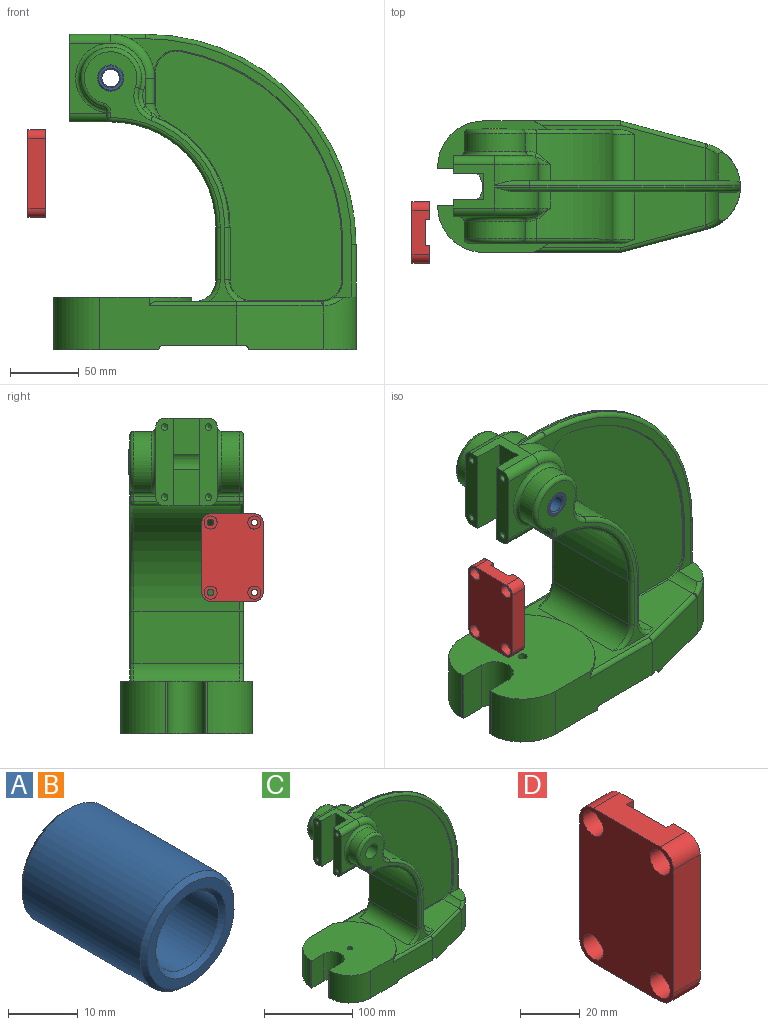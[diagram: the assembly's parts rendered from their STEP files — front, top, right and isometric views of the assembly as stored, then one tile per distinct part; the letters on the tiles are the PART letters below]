
ASSEMBLY  parts=4 mates=4
PART A: 8 faces, bbox 19.1x25.4x19.1 mm
  f0: plane 17.53x17.53mm, normal (0,-1,0), area 82.3mm2, adj f4,f5
  f1: plane 17.53x17.53mm, normal (0,1,0), area 82.3mm2, adj f6,f7
  f2: cylinder r=9.53mm len=23.88mm, axis (0,1,0), area 1428.9mm2, adj f4,f7
  f3: cylinder r=6.35mm len=23.88mm, axis (0,1,0), area 952.6mm2, adj f5,f6
  f4: cone r=9.53mm half-angle=45deg, axis (0,1,0), area 61.9mm2, adj f0,f2
  f5: cone r=6.35mm half-angle=45deg, axis (0,-1,0), area 45.6mm2, adj f0,f3
  f6: cone r=6.35mm half-angle=45deg, axis (0,1,0), area 45.6mm2, adj f1,f3
  f7: cone r=9.53mm half-angle=45deg, axis (0,-1,0), area 61.9mm2, adj f1,f2
PART B: same geometry as A
PART C: 180 faces, bbox 234.5x98.1x244 mm
  f0: plane 63.5x12.7mm, normal (-1,0,0), area 753.5mm2, adj f2,f15,f17,f92,f97,f149,f151,f158
  f1: plane 20.23x2.34mm, normal (0,1,0), area 23.9mm2, adj f90,f91,f104,f106
  f2: plane 50.8x30.1mm, normal (0,-1,0), area 515.4mm2, adj f0,f83,f92,f97,f124
  f3: plane 22.59x12.73mm, normal (1,0,0), area 235.4mm2, adj f19,f26,f32,f87,f94,f174
  f4: plane 22.59x12.73mm, normal (1,0,0), area 235.4mm2, adj f10,f14,f33,f86,f90,f164
  f5: plane 99.19x38.1mm, normal (0,-1,0), area 3202mm2, adj f6,f40,f46,f49,f52,f58,f76,f133
  f6: plane 100x95.25mm, normal (0,0,1), area 7398mm2, adj f5,f43,f44,f48,f54,f55,f56,f57
  f7: plane 38.1x34.96mm, normal (1,0,0), area 1331.9mm2, adj f8,f9,f114,f169
  f8: cylinder r=15.88mm len=34.96mm, axis (0,1,0), area 871.7mm2, adj f7,f37,f115,f167
  f9: cylinder r=85.72mm len=80.21mm, axis (0,1,0), area 3442.3mm2, adj f7,f80,f86,f100,f113,f168
  f10: cylinder r=15.88mm len=18.65mm, axis (0,1,0), area 22.7mm2, adj f4,f11,f33,f162
  f11: cylinder r=142.88mm len=140.67mm, axis (0,1,0), area 163.3mm2, adj f10,f12,f33,f160
  f12: plane 25.4x0.82mm, normal (-1,0,0), area 20.8mm2, adj f11,f13,f33,f161
  f13: cylinder r=15.88mm len=24.81mm, axis (0,1,0), area 242.1mm2, adj f12,f33,f37,f45,f139,f140,f163
  f14: cylinder r=31.75mm len=31.75mm, axis (0,1,0), area 616.8mm2, adj f4,f15,f33,f89,f141
  f15: plane 55.5x31.75mm, normal (0,0,1), area 573.2mm2, adj f0,f14,f16,f19,f31,f88,f92,f141
  f16: plane 63.5x12.7mm, normal (-1,0,0), area 753.5mm2, adj f15,f17,f21,f88,f96,f147,f153,f157
  f17: plane 31.75x30.1mm, normal (0,0,-1), area 533.2mm2, adj f0,f16,f18,f96,f97,f156,f157,f158
  f18: cylinder r=76.2mm len=76.2mm, axis (0,1,0), area 9120.7mm2, adj f17,f22,f103,f105,f119,f121
  f19: cylinder r=31.75mm len=31.75mm, axis (0,1,0), area 616.8mm2, adj f3,f15,f32,f93,f144
  f20: plane 20.23x2.34mm, normal (0,-1,0), area 23.9mm2, adj f94,f95,f122,f124
  f21: plane 50.8x30.1mm, normal (0,1,0), area 515.4mm2, adj f16,f78,f88,f96,f106
  f22: plane 76.2x38.1mm, normal (-1,0,0), area 2903.2mm2, adj f18,f98,f101,f117
  f23: cylinder r=15.88mm len=34.96mm, axis (0,1,0), area 871.7mm2, adj f24,f37,f132,f177
  f24: plane 38.1x34.96mm, normal (1,0,0), area 1331.9mm2, adj f23,f25,f131,f179
  f25: cylinder r=85.72mm len=80.21mm, axis (0,1,0), area 3442.3mm2, adj f24,f81,f87,f118,f130,f178
  f26: cylinder r=15.88mm len=18.65mm, axis (0,1,0), area 22.7mm2, adj f3,f27,f32,f172
  f27: cylinder r=142.88mm len=140.67mm, axis (0,1,0), area 163.3mm2, adj f26,f28,f32,f170
  f28: plane 25.4x0.82mm, normal (-1,0,0), area 20.8mm2, adj f27,f29,f32,f171
  f29: cylinder r=15.88mm len=24.81mm, axis (0,1,0), area 242.1mm2, adj f28,f32,f36,f37,f135,f136,f173
  f30: plane 76.2x7.92mm, normal (1,0,0), area 361.9mm2, adj f31,f36,f42,f45,f51,f53,f143,f146
  f31: cylinder r=152.4mm len=152.4mm, axis (0,1,0), area 377mm2, adj f15,f30,f142,f145
  f32: plane 187.33x160.79mm, normal (0,-1,0), area 1900.4mm2, adj f3,f19,f26,f27,f28,f29,f36,f144
  f33: plane 187.33x160.79mm, normal (0,1,0), area 1900.4mm2, adj f4,f10,f11,f12,f13,f14,f45,f141
  f34: plane 180.67x135mm, normal (0,-1,0), area 14138.8mm2, adj f170,f171,f172,f173,f174,f175,f176,f177
  f35: plane 180.67x135mm, normal (0,1,0), area 14138.8mm2, adj f160,f161,f162,f163,f164,f165,f166,f167
  f36: plane 26.58x18.73mm, normal (0,0,1), area 245.8mm2, adj f29,f30,f32,f53,f136,f146
  f37: plane 119.12x89.67mm, normal (0,0,1), area 4280.2mm2, adj f8,f13,f23,f29,f76,f77,f84,f98
  f38: cylinder r=3.17mm len=9.06mm, axis (0,1,0), area 40.9mm2, adj f40,f42,f52,f69
  f39: cylinder r=3.17mm len=7.93mm, axis (0,1,0), area 39.5mm2, adj f41,f46,f48,f65
  f40: plane 58.73x9.7mm, normal (0,0,-1), area 467.1mm2, adj f5,f38,f49,f52,f64,f69
  f41: plane 58.73x9.7mm, normal (0,0,-1), area 467.1mm2, adj f39,f47,f48,f50,f65,f67
  f42: plane 90.55x77.8mm, normal (0,0,-1), area 1454mm2, adj f30,f38,f47,f50,f51,f52,f53,f59
  f43: plane 38.1x1.61mm, normal (-1,0,0), area 61.5mm2, adj f6,f46,f54,f58
  f44: plane 38.1x1.61mm, normal (-1,0,0), area 61.5mm2, adj f6,f46,f55,f57
  f45: plane 26.58x18.73mm, normal (0,0,1), area 245.8mm2, adj f13,f30,f33,f51,f140,f143
  f46: plane 95.25x76.2mm, normal (0,0,-1), area 2029.8mm2, adj f5,f39,f43,f44,f48,f49,f54,f55
  f47: cylinder r=3.17mm len=9.06mm, axis (0,1,0), area 40.9mm2, adj f41,f42,f50,f67
  f48: plane 99.19x38.1mm, normal (0,1,0), area 3202mm2, adj f6,f39,f41,f46,f50,f57,f76,f137
  f49: cylinder r=3.17mm len=7.93mm, axis (0,1,0), area 39.5mm2, adj f5,f40,f46,f64
  f50: plane 63.64x32.15mm, normal (0.26,0.97,0), area 2053.6mm2, adj f41,f42,f47,f48,f51,f138,f139
  f51: cylinder r=31.75mm len=38.1mm, axis (0,0,-1), area 1379.2mm2, adj f30,f42,f45,f50,f140
  f52: plane 63.64x32.15mm, normal (0.26,-0.97,0), area 2053.6mm2, adj f5,f38,f40,f42,f53,f134,f135
  f53: cylinder r=31.75mm len=38.1mm, axis (0,0,-1), area 1379.2mm2, adj f30,f36,f42,f52,f136
  f54: plane 38.1x19.05mm, normal (0,1,0), area 725.8mm2, adj f6,f43,f46,f56
  f55: plane 38.1x19.05mm, normal (0,-1,0), area 725.8mm2, adj f6,f44,f46,f56
  f56: cylinder r=13.49mm len=38.1mm, axis (0,0,-1), area 1615.1mm2, adj f6,f46,f54,f55
  f57: cylinder r=33.32mm len=38.1mm, axis (0,0,-1), area 1963.7mm2, adj f6,f44,f46,f48
  f58: cylinder r=33.32mm len=38.1mm, axis (0,0,-1), area 1963.7mm2, adj f5,f6,f43,f46
  f59: plane 30.18x6.86mm, normal (-1,0,0), area 207mm2, adj f42,f60,f68,f70
  f60: plane 31.27x5.6mm, normal (0,0,-1), area 124.1mm2, adj f59,f61,f68,f70
  f61: cylinder r=23.8mm len=46.06mm, axis (0,1,0), area 499.2mm2, adj f60,f62,f67,f68,f69,f70
  f62: plane 84.13x79.4mm, normal (0,0,-1), area 5642.5mm2, adj f61,f64,f65,f66,f67,f69
  f63: plane 100.62x79.4mm, normal (0,0,-1), area 6568.5mm2, adj f64,f65,f66,f71,f72,f73,f74,f75
  f64: plane 98.15x30.18mm, normal (0,1,0), area 2718.8mm2, adj f40,f46,f49,f62,f63,f66,f69,f75
  f65: plane 98.15x30.18mm, normal (0,-1,0), area 2718.8mm2, adj f39,f41,f46,f62,f63,f66,f67,f74
  f66: plane 79.4x3.18mm, normal (-1,0,0), area 252.1mm2, adj f62,f63,f64,f65
  f67: plane 62.63x27.36mm, normal (-0.26,-0.97,0), area 1710.8mm2, adj f41,f42,f47,f61,f62,f65,f68
  f68: cylinder r=23.83mm len=30.18mm, axis (0,0,-1), area 814.8mm2, adj f42,f59,f60,f61,f67
  f69: plane 62.63x27.36mm, normal (-0.26,0.97,0), area 1710.8mm2, adj f38,f40,f42,f61,f62,f64,f70
  f70: cylinder r=23.83mm len=30.18mm, axis (0,0,-1), area 814.8mm2, adj f42,f59,f60,f61,f69
  f71: plane 30.18x10.12mm, normal (0,-1,0), area 305.3mm2, adj f46,f63,f73,f75
  f72: plane 30.18x10.12mm, normal (0,1,0), area 305.3mm2, adj f46,f63,f73,f74
  f73: cylinder r=21.42mm len=42.84mm, axis (0,0,-1), area 2030.4mm2, adj f46,f63,f71,f72
  f74: cylinder r=25.4mm len=30.18mm, axis (0,0,-1), area 986.2mm2, adj f46,f63,f65,f72
  f75: cylinder r=25.4mm len=30.18mm, axis (0,0,-1), area 986.2mm2, adj f46,f63,f64,f71
  f76: cylinder r=52.37mm len=95.25mm, axis (0,0,1), area 401mm2, adj f5,f6,f37,f48,f133,f137
  f77: plane 180.98x110.12mm, normal (0,1,0), area 1717.8mm2, adj f37,f85,f99,f101,f103,f109,f110,f111
  f78: plane 16.73x3.98mm, normal (-1,0,0), area 64.1mm2, adj f21,f96,f105,f106,f108,f109
  f79: cylinder r=22.23mm len=44.45mm, axis (0,1,0), area 1356.2mm2, adj f80,f106,f108,f111
  f80: cylinder r=15.88mm len=20.22mm, axis (0,1,0), area 319.4mm2, adj f9,f79,f102,f104,f112
  f81: cylinder r=15.88mm len=20.22mm, axis (0,1,0), area 319.4mm2, adj f25,f82,f120,f122,f129
  f82: cylinder r=22.23mm len=44.45mm, axis (0,1,0), area 1356.2mm2, adj f81,f124,f126,f128
  f83: plane 16.73x3.98mm, normal (-1,0,0), area 64.1mm2, adj f2,f97,f121,f124,f125,f126
  f84: plane 180.98x110.12mm, normal (0,-1,0), area 1717.8mm2, adj f37,f85,f116,f117,f119,f125,f127,f128
  f85: cylinder r=9.53mm len=82.55mm, axis (0,1,0), area 4727mm2, adj f77,f84,f156,f157,f158,f159
  f86: cylinder r=15.88mm len=14.02mm, axis (0,1,0), area 218.9mm2, adj f4,f9,f91,f166
  f87: cylinder r=15.88mm len=14.02mm, axis (0,1,0), area 218.9mm2, adj f3,f25,f95,f176
  f88: cylinder r=6.35mm len=30.1mm, axis (-1,0,0), area 300.2mm2, adj f15,f16,f21,f89
  f89: torus R=25.4mm, axis (0,-1,0), area 461.3mm2, adj f14,f88,f90,f106
  f90: cylinder r=6.35mm len=18.2mm, axis (0,0,1), area 181.6mm2, adj f1,f4,f89,f91
  f91: torus R=22.23mm, axis (0,-1,0), area 98mm2, adj f1,f86,f90,f100,f102
  f92: cylinder r=6.35mm len=30.1mm, axis (1,0,0), area 300.2mm2, adj f0,f2,f15,f93
  f93: torus R=25.4mm, axis (0,-1,0), area 461.3mm2, adj f19,f92,f94,f124
  f94: cylinder r=6.35mm len=18.2mm, axis (0,0,-1), area 181.6mm2, adj f3,f20,f93,f95
  f95: torus R=22.23mm, axis (0,-1,0), area 98mm2, adj f20,f87,f94,f118,f120
  f96: cylinder r=6.35mm len=30.1mm, axis (1,0,0), area 279.1mm2, adj f16,f17,f21,f78,f105
  f97: cylinder r=6.35mm len=30.1mm, axis (-1,0,0), area 279.1mm2, adj f0,f2,f17,f83,f121
  f98: cylinder r=15.88mm len=76.2mm, axis (0,-1,0), area 1900.2mm2, adj f22,f37,f99,f116
  f99: torus R=19.05mm, axis (0,-1,0), area 107.7mm2, adj f37,f77,f98,f101
  f100: bspline ~12.01x8.85mm, area 17.9mm2, adj f9,f91,f102
  f101: cylinder r=3.17mm len=38.1mm, axis (0,0,-1), area 190mm2, adj f22,f77,f99,f103
  f102: bspline ~10.6x9.56mm, area 36.6mm2, adj f80,f91,f100,f104
  f103: torus R=79.38mm, axis (0,-1,0), area 606mm2, adj f18,f77,f101,f107
  f104: torus R=12.7mm, axis (0,-1,0), area 70.6mm2, adj f1,f80,f102,f106
  f105: cylinder r=3.17mm len=22.23mm, axis (0,1,0), area 97.1mm2, adj f18,f78,f96,f107
  f106: torus R=25.4mm, axis (0,-1,0), area 570mm2, adj f1,f21,f78,f79,f89,f104,f108
  f107: sphere r=3.17mm, area 21.6mm2, adj f103,f105,f109
  f108: cylinder r=3.17mm len=15.82mm, axis (0,1,0), area 59.7mm2, adj f78,f79,f106,f110
  f109: cylinder r=3.17mm len=3.98mm, axis (0,0,-1), area 19.9mm2, adj f77,f78,f107,f110
  f110: torus R=6.35mm, axis (0,-1,0), area 28.5mm2, adj f77,f108,f109,f111
  f111: torus R=19.05mm, axis (0,-1,0), area 504.9mm2, adj f77,f79,f110,f112
  f112: torus R=19.05mm, axis (0,-1,0), area 132.1mm2, adj f77,f80,f111,f113
  f113: torus R=82.55mm, axis (0,-1,0), area 510.4mm2, adj f9,f77,f112,f114
  f114: cylinder r=3.17mm len=38.1mm, axis (0,0,1), area 190mm2, adj f7,f77,f113,f115
  f115: torus R=19.05mm, axis (0,-1,0), area 107.7mm2, adj f8,f37,f77,f114
  f116: torus R=19.05mm, axis (0,-1,0), area 107.7mm2, adj f37,f84,f98,f117
  f117: cylinder r=3.17mm len=38.1mm, axis (0,0,1), area 190mm2, adj f22,f84,f116,f119
  f118: bspline ~11.06x8.44mm, area 17.9mm2, adj f25,f95,f120
  f119: torus R=79.38mm, axis (0,-1,0), area 606mm2, adj f18,f84,f117,f123
  f120: bspline ~9.12x8.99mm, area 36.6mm2, adj f81,f95,f118,f122
  f121: cylinder r=3.17mm len=22.23mm, axis (0,1,0), area 97.1mm2, adj f18,f83,f97,f123
  f122: torus R=12.7mm, axis (0,-1,0), area 70.6mm2, adj f20,f81,f120,f124
  f123: sphere r=3.17mm, area 15.8mm2, adj f119,f121,f125
  f124: torus R=25.4mm, axis (0,-1,0), area 570mm2, adj f2,f20,f82,f83,f93,f122,f126
  f125: cylinder r=3.17mm len=3.98mm, axis (0,0,1), area 19.9mm2, adj f83,f84,f123,f127
  f126: cylinder r=3.17mm len=15.82mm, axis (0,1,0), area 59.7mm2, adj f82,f83,f124,f127
  f127: torus R=6.35mm, axis (0,-1,0), area 28.5mm2, adj f84,f125,f126,f128
  f128: torus R=19.05mm, axis (0,-1,0), area 504.9mm2, adj f82,f84,f127,f129
  f129: torus R=19.05mm, axis (0,-1,0), area 132.1mm2, adj f81,f84,f128,f130
  f130: torus R=82.55mm, axis (0,-1,0), area 510.4mm2, adj f25,f84,f129,f131
  f131: cylinder r=3.17mm len=38.1mm, axis (0,0,-1), area 190mm2, adj f24,f84,f130,f132
  f132: torus R=19.05mm, axis (0,-1,0), area 107.7mm2, adj f23,f37,f84,f131
  f133: cylinder r=3.17mm len=63.09mm, axis (1,0,0), area 298.9mm2, adj f5,f37,f76,f134
  f134: cylinder r=3.17mm len=62.81mm, axis (0.97,0.26,0), area 319mm2, adj f37,f52,f133,f135
  f135: bspline ~3.41x3.21mm, area 6mm2, adj f29,f52,f134,f136
  f136: bspline ~18.95x11.92mm, area 79.7mm2, adj f29,f36,f53,f135
  f137: cylinder r=3.17mm len=63.09mm, axis (-1,0,0), area 298.9mm2, adj f37,f48,f76,f138
  f138: cylinder r=3.17mm len=62.81mm, axis (-0.97,0.26,0), area 319mm2, adj f37,f50,f137,f139
  f139: bspline ~6.89x4.84mm, area 6mm2, adj f13,f50,f138,f140
  f140: bspline ~17.46x11.57mm, area 79.7mm2, adj f13,f45,f51,f139
  f141: cylinder r=3.17mm len=25.4mm, axis (-1,0,0), area 92.2mm2, adj f14,f15,f33,f142
  f142: torus R=149.22mm, axis (0,-1,0), area 1184.9mm2, adj f31,f33,f141,f143
  f143: cylinder r=3.17mm len=38.1mm, axis (0,0,1), area 190mm2, adj f30,f33,f45,f142
  f144: cylinder r=3.17mm len=25.4mm, axis (1,0,0), area 92.2mm2, adj f15,f19,f32,f145
  f145: torus R=149.22mm, axis (0,-1,0), area 1184.9mm2, adj f31,f32,f144,f146
  f146: cylinder r=3.17mm len=38.1mm, axis (0,0,-1), area 190mm2, adj f30,f32,f36,f145
  f147: cylinder r=2.38mm len=6.35mm, axis (-1,0,0), area 95mm2, adj f16,f148
  f148: cone r=0mm half-angle=59deg, axis (-1,0,0), area 20.8mm2, adj f147
  f149: cylinder r=2.38mm len=6.35mm, axis (-1,0,0), area 95mm2, adj f0,f150
  f150: cone r=0mm half-angle=59deg, axis (-1,0,0), area 20.8mm2, adj f149
  f151: cylinder r=2.38mm len=6.35mm, axis (-1,0,0), area 95mm2, adj f0,f152
  f152: cone r=0mm half-angle=59deg, axis (-1,0,0), area 20.8mm2, adj f151
  f153: cylinder r=2.38mm len=6.35mm, axis (-1,0,0), area 95mm2, adj f16,f154
  f154: cone r=0mm half-angle=59deg, axis (-1,0,0), area 20.8mm2, adj f153
  f155: cylinder r=3.17mm len=7.93mm, axis (0,0,1), area 158.1mm2, adj f6,f63
  f156: plane 26.47x19.05mm, normal (-1,0,0), area 504.2mm2, adj f17,f85,f157,f158
  f157: plane 63.5x22.17mm, normal (0,-1,0), area 1396.6mm2, adj f15,f16,f17,f85,f156,f159
  f158: plane 63.5x22.17mm, normal (0,1,0), area 1396.6mm2, adj f0,f15,f17,f85,f156,f159
  f159: plane 26.47x19.05mm, normal (-1,0,0), area 504.2mm2, adj f15,f85,f157,f158
  f160: torus R=142.11mm, axis (0,-1,0), area 238.1mm2, adj f11,f35,f161,f162
  f161: cylinder r=0.76mm len=25.4mm, axis (0,0,1), area 30.4mm2, adj f12,f35,f160,f163
  f162: torus R=15.11mm, axis (0,-1,0), area 32.6mm2, adj f10,f35,f160,f164
  f163: torus R=15.11mm, axis (0,-1,0), area 29.3mm2, adj f13,f35,f161,f165
  f164: cylinder r=0.76mm len=22.59mm, axis (0,0,1), area 27mm2, adj f4,f35,f162,f166
  f165: cylinder r=0.76mm len=50.8mm, axis (1,0,0), area 60.8mm2, adj f35,f37,f163,f167
  f166: torus R=15.11mm, axis (0,-1,0), area 20.2mm2, adj f35,f86,f164,f168
  f167: torus R=15.11mm, axis (0,-1,0), area 29.3mm2, adj f8,f35,f165,f169
  f168: torus R=86.49mm, axis (0,-1,0), area 111.5mm2, adj f9,f35,f166,f169
  f169: cylinder r=0.76mm len=38.1mm, axis (0,0,-1), area 45.6mm2, adj f7,f35,f167,f168
  f170: torus R=142.11mm, axis (0,-1,0), area 238.1mm2, adj f27,f34,f171,f172
  f171: cylinder r=0.76mm len=25.4mm, axis (0,0,-1), area 30.4mm2, adj f28,f34,f170,f173
  f172: torus R=15.11mm, axis (0,-1,0), area 32.6mm2, adj f26,f34,f170,f174
  f173: torus R=15.11mm, axis (0,-1,0), area 29.3mm2, adj f29,f34,f171,f175
  f174: cylinder r=0.76mm len=22.59mm, axis (0,0,-1), area 27mm2, adj f3,f34,f172,f176
  f175: cylinder r=0.76mm len=50.8mm, axis (-1,0,0), area 60.8mm2, adj f34,f37,f173,f177
  f176: torus R=15.11mm, axis (0,-1,0), area 20.2mm2, adj f34,f87,f174,f178
  f177: torus R=15.11mm, axis (0,-1,0), area 29.3mm2, adj f23,f34,f175,f179
  f178: torus R=86.49mm, axis (0,-1,0), area 111.5mm2, adj f25,f34,f176,f179
  f179: cylinder r=0.76mm len=38.1mm, axis (0,0,1), area 45.6mm2, adj f24,f34,f177,f178
PART D: 26 faces, bbox 12.7x44.5x63.5 mm
  f0: plane 63.5x12.7mm, normal (1,0,0), area 753.5mm2, adj f1,f2,f6,f7,f8,f14,f17,f25
  f1: cylinder r=6.35mm len=12.7mm, axis (1,0,0), area 126.7mm2, adj f0,f2,f8,f9
  f2: plane 31.75x12.7mm, normal (0,0,1), area 341.8mm2, adj f0,f1,f3,f9,f10,f23,f24,f25
  f3: cylinder r=6.35mm len=12.7mm, axis (1,0,0), area 126.7mm2, adj f2,f4,f9,f10
  f4: plane 50.8x12.7mm, normal (0,1,0), area 645.2mm2, adj f3,f5,f9,f10
  f5: cylinder r=6.35mm len=12.7mm, axis (1,0,0), area 126.7mm2, adj f4,f6,f9,f10
  f6: plane 31.75x12.7mm, normal (0,0,-1), area 341.8mm2, adj f0,f5,f7,f9,f10,f23,f24,f25
  f7: cylinder r=6.35mm len=12.7mm, axis (1,0,0), area 126.7mm2, adj f0,f6,f8,f9
  f8: plane 50.8x12.7mm, normal (0,-1,0), area 645.2mm2, adj f0,f1,f7,f9
  f9: plane 63.5x44.45mm, normal (-1,0,0), area 2502.9mm2, adj f1,f2,f3,f4,f5,f6,f7,f8
  f10: plane 63.5x12.7mm, normal (1,0,0), area 753.5mm2, adj f2,f3,f4,f5,f6,f11,f20,f24
  f11: cylinder r=2.38mm len=6.35mm, axis (-1,0,0), area 95mm2, adj f10,f12
  f12: plane 9.53x9.53mm, normal (-1,0,0), area 53.4mm2, adj f11,f13
  f13: cylinder r=4.76mm len=9.53mm, axis (-1,0,0), area 190mm2, adj f9,f12
  f14: cylinder r=2.38mm len=6.35mm, axis (-1,0,0), area 95mm2, adj f0,f15
  f15: plane 9.53x9.53mm, normal (-1,0,0), area 53.4mm2, adj f14,f16
  f16: cylinder r=4.76mm len=9.53mm, axis (-1,0,0), area 190mm2, adj f9,f15
  f17: cylinder r=2.38mm len=6.35mm, axis (-1,0,0), area 95mm2, adj f0,f18
  f18: plane 9.53x9.53mm, normal (-1,0,0), area 53.4mm2, adj f17,f19
  f19: cylinder r=4.76mm len=9.53mm, axis (-1,0,0), area 190mm2, adj f9,f18
  f20: cylinder r=2.38mm len=6.35mm, axis (-1,0,0), area 95mm2, adj f10,f21
  f21: plane 9.53x9.53mm, normal (-1,0,0), area 53.4mm2, adj f20,f22
  f22: cylinder r=4.76mm len=9.53mm, axis (-1,0,0), area 190mm2, adj f9,f21
  f23: plane 63.5x19.05mm, normal (1,0,0), area 1209.7mm2, adj f2,f6,f24,f25
  f24: plane 63.5x3.23mm, normal (0,-1,0), area 204.8mm2, adj f2,f6,f10,f23
  f25: plane 63.5x3.23mm, normal (0,1,0), area 204.8mm2, adj f0,f2,f6,f23
PLACE A t=(0.08,-48.04,71.18)mm
PLACE B t=(0.08,9.87,71.18)mm
PLACE C t=(0.08,9.11,71.18)mm
PLACE D t=(-17.09,-24.16,1.98)mm
MATE fastened B.f2 <-> C.f14  axis (0,1,0) through (0.08,50.39,71.18)mm
MATE fastened A.f2 <-> C.f14  axis (0,-1,0) through (0.08,-32.16,71.18)mm
MATE fastened C.f77 <-> B.f2  axis (0,1,0) through (25.43,50.39,34.51)mm
MATE fastened B.f2 <-> C.f77  axis (0,1,0) through (0.08,51.15,71.18)mm
